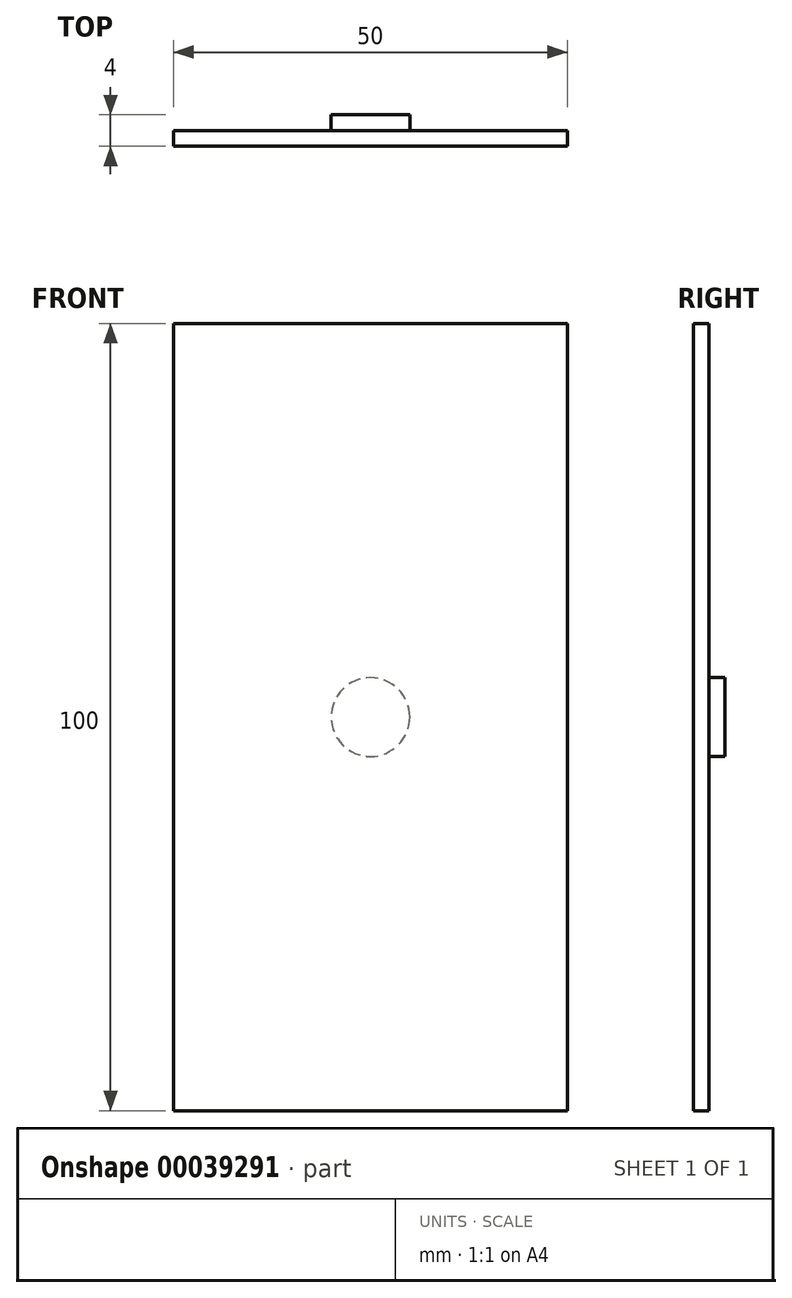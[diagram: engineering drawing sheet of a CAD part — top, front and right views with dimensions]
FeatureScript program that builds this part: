
annotation { "Feature Type Name" : "Feature", "Feature Type Description" : "" }
export const myFeature = defineFeature(function(context is Context, id is Id, definition is map)
    precondition{}
    {
        {
            var Q0;
            Q0=qCreatedBy(makeId("Front.planeOp"),FACE);
            var sketch = newSketch(context, id + "F0", { "sketchPlane" : qUnion([Q0])});
            skCircle(sketch, "E0", {"center": v(0, 0) * mm, "radius": 5 * mm});
            skSolve(sketch);
        }
        {
            var Q0;
            Q0 = qSketchRegion(id + "F0", true);
            extrude(context, id + "F1", {"entities" : qUnion([Q0]), "depth" : 2 * mm});
        }
        {
            var Q0;
            Q0=makeQuery(id+"F1.opExtrude","CAP_FACE",FACE,{"disambiguationData":[OSD([sQuery(id+"F0.wireOp",EDGE,"E0")])],"isStart":false});
            var sketch = newSketch(context, id + "F2", { "sketchPlane" : qUnion([Q0])});
            skLineSegment(sketch, "E1.rect.bottom", {"start": v(25, 50) * mm, "end": v(-25, 50) * mm});
            skLineSegment(sketch, "E1.rect.top", {"start": v(25, -50) * mm, "end": v(-25, -50) * mm});
            skLineSegment(sketch, "E1.rect.left", {"start": v(25, 50) * mm, "end": v(25, -50) * mm});
            skLineSegment(sketch, "E1.rect.right", {"start": v(-25, 50) * mm, "end": v(-25, -50) * mm});
            skPoint(sketch, "E1.rect.middle", {"position": v(0, 0) * mm});
            skSolve(sketch);
        }
        {
            var Q0;
            Q0 = qSketchRegion(id + "F2", true);
            extrude(context, id + "F3", {"entities" : qUnion([Q0]), "operationType" : NewBodyOperationType.ADD, "depth" : 2 * mm});
        }
    });
